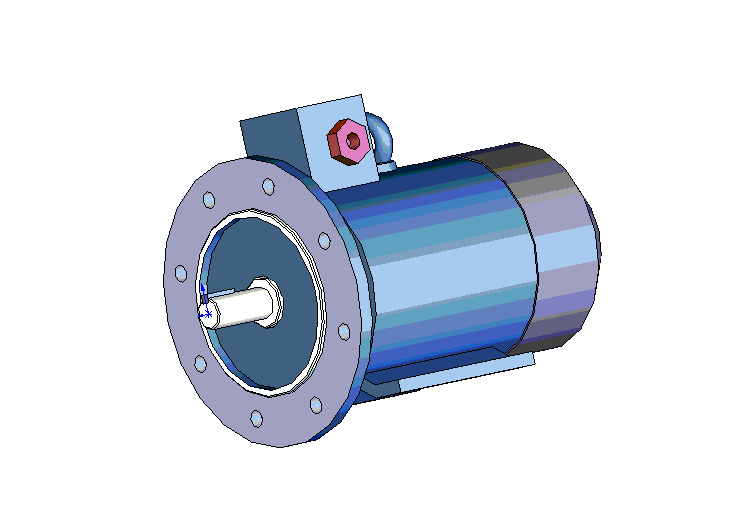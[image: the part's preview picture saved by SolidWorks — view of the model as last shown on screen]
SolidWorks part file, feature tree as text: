
SOLIDWORKS PART (.sldprt)
format: sldprt  version: not decoded by parser v0  size: 743,424 bytes
history: native  units: mm
features: sketch x18, extrude x12, plane x4, chamfer x4, cut_extrude x4, material x1, sweep x1 (+10 scaffold rows collapsed)
feature tree (54):
  scaffold x10  (default folders/planes/origin — collapsed)
  material  "Ст.3 ГОСТ 380-88"
  plane  "Спереди"
  plane  "Сверху"
  plane  "Справа"
  sketch  "Эскиз1"  dims[D1=22.0mm]
  extrude  "Вытянуть1"  Depth=50mm
  sketch  "Эскиз2"  dims[D1=6.0mm D2=6.0mm D3=24.5mm]
  extrude  "Вытянуть2"  Depth=25mm
  chamfer  "Фаска1"  Distance=1mm Angle=45deg
  sketch  "Эскиз3"  dims[D1=200.0mm]
  extrude  "Вытянуть3"  Depth=10mm
  sketch  "Эскиз4"  dims[D1=130.0mm D2=120.0mm]
  extrude  "Вытянуть4"  Depth=3.5mm
  sketch  "Эскиз5"  dims[D1=120.0mm D2=36.0mm]
  cut_extrude  "Вырез-Вытянуть1"  Depth=3.5mm
  chamfer  "Фаска2"  Distance=1mm Angle=45deg
  sketch  "Эскиз6"  dims[D1=130.0mm]
  extrude  "Вытянуть5"  Depth=30mm
  sketch  "Эскиз7"  dims[D1=142.0mm]
  extrude  "Вытянуть6"  Depth=149mm
  sketch  "Эскиз8"  dims[D1=~144.496182mm]
  extrude  "Вытянуть7"  Depth=81.5mm
  chamfer  "Фаска3"  Distance=26mm Angle=45deg
  sketch  "Эскиз9"  dims[c1.D2=12.0mm c1.D4=12.0mm c1.D1=~128.009757mm c2.D1=22.5deg c2.D3=82.5mm c2.D4=82.5mm c2.D5=82.5mm]
  cut_extrude  "Вырез-Вытянуть2"  [1 undecoded]
  sketch  "Эскиз10"  dims[c1.D1=9.0mm c1.D2=74.5mm c1.D3=24.0mm c1.D4=9.0mm c1.D5=~41.087468mm c2.D5=60.0deg c2.D6=80.0mm]
  extrude  "Вытянуть8"  Depth=124mm
  sketch  "Эскиз11"  dims[D2=10.0mm D1=100.0mm D3=62.5mm D4=90.0deg D5=200.0mm D6=100.0mm D7=125.0mm]
  cut_extrude  "Вырез-Вытянуть3"  [1 undecoded]
  sketch  "Эскиз12"  dims[D1=60.0mm D2=1.0mm D3=60.0mm]
  extrude  "Вытянуть9"  Depth=124.5mm
  sketch  "Эскиз13"  dims[D1=30.0mm D2=175.0mm]
  extrude  "Вытянуть10"  Depth=76.5mm
  chamfer  "Фаска4"  Distance=1mm Angle=45deg
  plane  "Плоскость1"  Offset=175mm
  sketch  "Эскиз14"  dims[D1=30.0mm]
  sketch  "Эскиз15"  dims[D1=12.0mm D2=15.0mm]
  sweep  "По траектории1"
  sketch  "Эскиз16"  dims[D1=16.0mm D2=30.0mm D3=30.0mm]
  extrude  "Вытянуть11"  Depth=6mm
  sketch  "Эскиз17"  dims[D1=30.0mm]
  extrude  "Вытянуть12"  Depth=10mm
  sketch  "Эскиз18"  dims[D1=12.0mm]
  cut_extrude  "Вырез-Вытянуть4"  Depth=10mm
decode coverage: 36 of 39 modeling features carry decoded parameters
note: ~ marks probable driven/reference dimensions
note: 2 parameter values undecoded
note: suppression state not decoded; provenance and decode notes live in map.json
